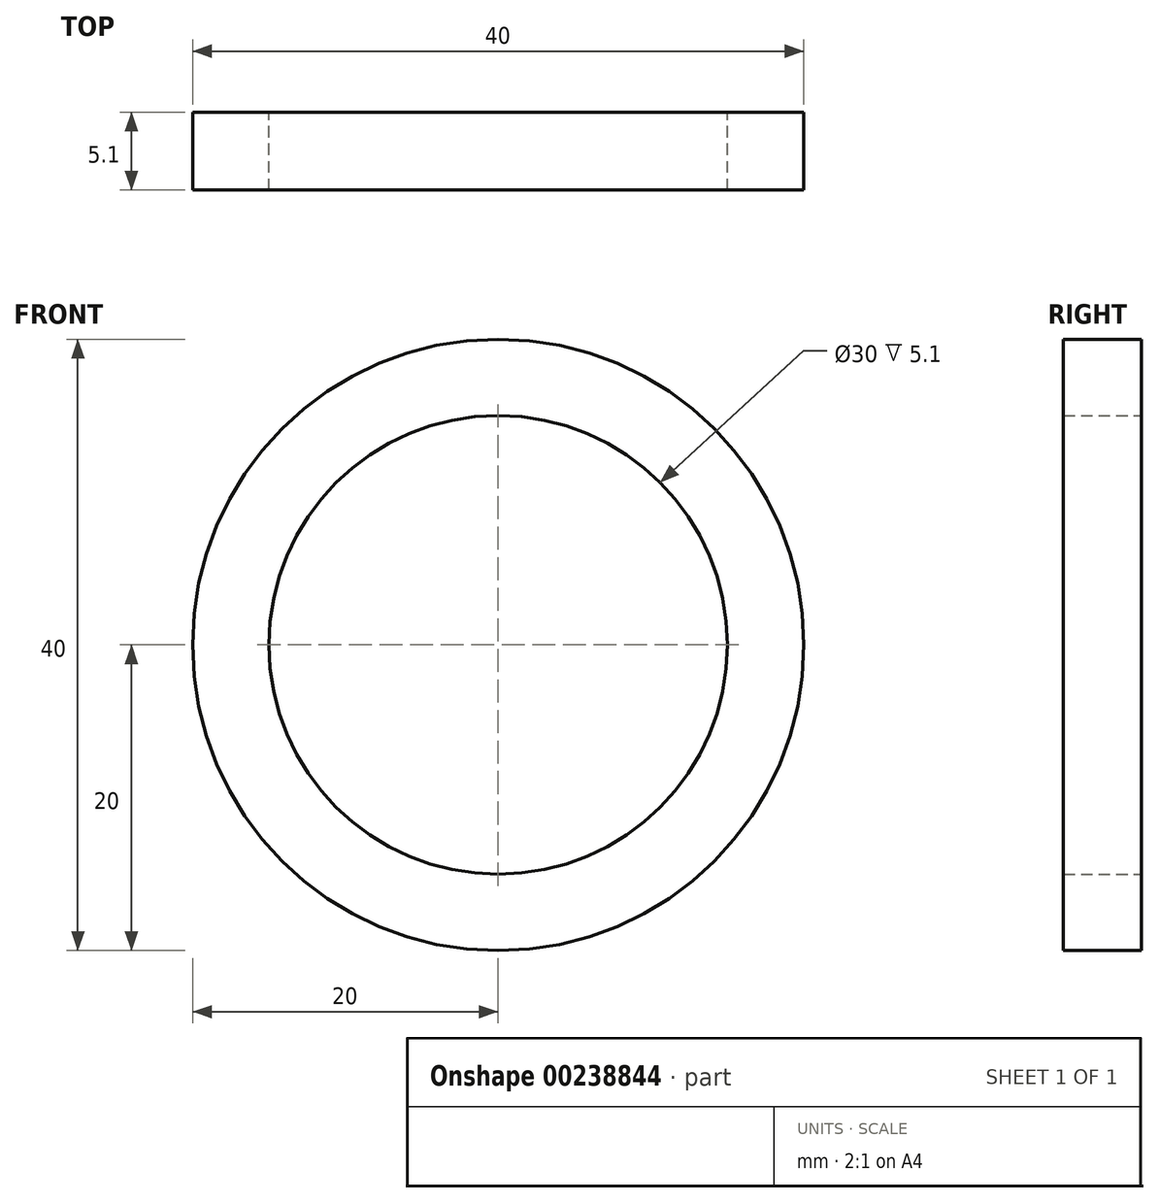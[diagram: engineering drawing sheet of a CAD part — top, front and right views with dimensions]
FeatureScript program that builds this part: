
annotation { "Feature Type Name" : "Feature", "Feature Type Description" : "" }
export const myFeature = defineFeature(function(context is Context, id is Id, definition is map)
    precondition{}
    {
        {
            var Q0;
            Q0=qCreatedBy(makeId("Front.planeOp"),FACE);
            var sketch = newSketch(context, id + "F0", { "sketchPlane" : qUnion([Q0])});
            skCircle(sketch, "E0", {"center": v(0, 0) * mm, "radius": 15 * mm});
            skCircle(sketch, "E1", {"center": v(0, 0) * mm, "radius": 20 * mm});
            skSolve(sketch);
        }
        {
            var Q0;
            Q0=makeQuery(id+"F0.imprint","IMPRINT",FACE,{"disambiguationData":[TD([[makeQuery(id+"F0.imprint","IMPRINT",EDGE,{"derivedFrom":sQuery(id+"F0.wireOp",EDGE,"E0")}),-1.0]])]});
            extrude(context, id + "F1", {"entities" : qUnion([Q0]), "depth" : 5.1 * mm});
        }
    });
